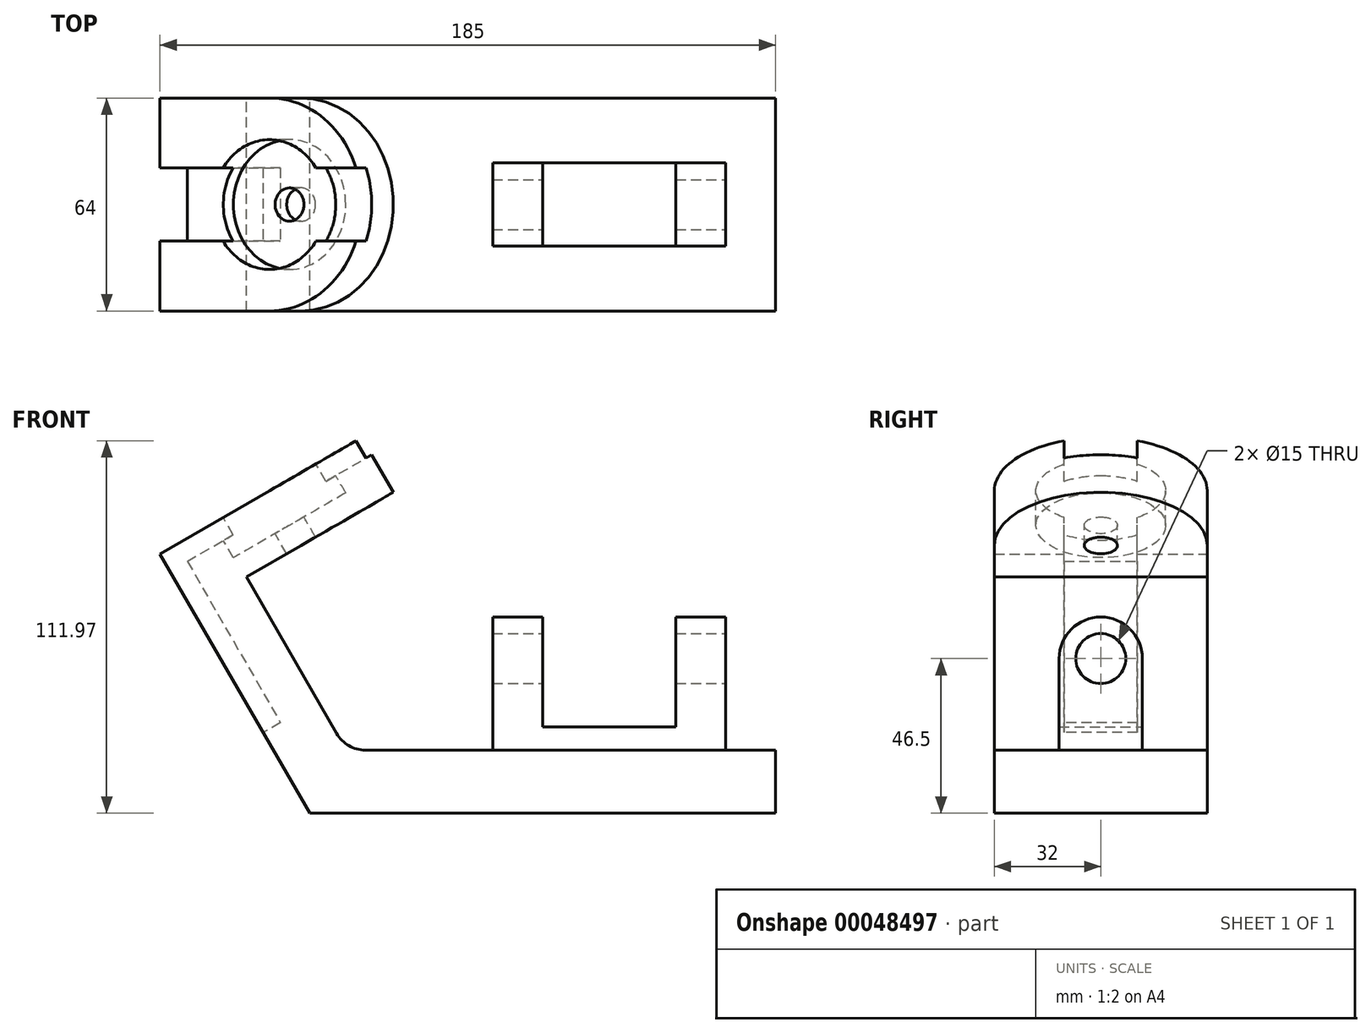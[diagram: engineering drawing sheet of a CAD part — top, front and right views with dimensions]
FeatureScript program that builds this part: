
annotation { "Feature Type Name" : "Feature", "Feature Type Description" : "" }
export const myFeature = defineFeature(function(context is Context, id is Id, definition is map)
    precondition{}
    {
        {
            var Q0;
            Q0=qCreatedBy(makeId("Front.planeOp"),FACE);
            var sketch = newSketch(context, id + "F0", { "sketchPlane" : qUnion([Q0])});
            skLineSegment(sketch, "E0", {"start": v(0, 0) * mm, "end": v(140, 0) * mm});
            skLineSegment(sketch, "E1", {"start": v(0, 0) * mm, "end": v(-45, 77.94) * mm});
            skLineSegment(sketch, "E2", {"start": v(-45, 77.94) * mm, "end": v(15.62, 112.94) * mm});
            skLineSegment(sketch, "E3.0", {"start": v(-19.05, 70.99) * mm, "end": v(25.12, 96.49) * mm});
            skLineSegment(sketch, "E3.1", {"start": v(10.97, 19) * mm, "end": v(-19.05, 70.99) * mm});
            skLineSegment(sketch, "E3.2", {"start": v(10.97, 19) * mm, "end": v(140, 19) * mm});
            skLineSegment(sketch, "E4", {"start": v(15.62, 112.94) * mm, "end": v(25.12, 96.49) * mm});
            skLineSegment(sketch, "E5", {"start": v(140, 19) * mm, "end": v(140, 0) * mm});
            skLineSegment(sketch, "E6", {"start": v(125, 19) * mm, "end": v(125, 59) * mm});
            skLineSegment(sketch, "E7", {"start": v(125, 59) * mm, "end": v(110, 59) * mm});
            skLineSegment(sketch, "E8", {"start": v(110, 59) * mm, "end": v(110, 26) * mm});
            skLineSegment(sketch, "E9", {"start": v(110, 26) * mm, "end": v(70, 26) * mm});
            skLineSegment(sketch, "E10", {"start": v(70, 26) * mm, "end": v(70, 59) * mm});
            skLineSegment(sketch, "E11", {"start": v(70, 59) * mm, "end": v(55, 59) * mm});
            skLineSegment(sketch, "E12", {"start": v(55, 59) * mm, "end": v(55, 19) * mm});
            skSolve(sketch);
        }
        {
            var Q0;
            Q0=makeQuery(id+"F0.imprint","IMPRINT",FACE,{"disambiguationData":[TD([[makeQuery(id+"F0.imprint","IMPRINT",EDGE,{"derivedFrom":sQuery(id+"F0.wireOp",EDGE,"E0")}),1.0]])]});
            extrude(context, id + "F1", {"entities" : qUnion([Q0]), "endBound" : BoundingType.SYMMETRIC, "depth" : 64 * mm});
        }
        {
            var Q0;
            {var subQ2=sQuery(id+"F0.wireOp",EDGE,"E6");Q0=makeQuery(id+"F0.imprint","IMPRINT",FACE,{"disambiguationData":[TD([[makeQuery(id+"F0.imprint","IMPRINT",EDGE,{"derivedFrom":subQ2}),1.0]])]});}
            extrude(context, id + "F2", {"entities" : qUnion([Q0]), "operationType" : NewBodyOperationType.ADD, "endBound" : BoundingType.SYMMETRIC, "depth" : 25 * mm});
        }
        {
            var Q0;
            Q0=makeQuery(id+"F1.opExtrude","SWEPT_FACE",FACE,{"disambiguationData":[OSD([sQuery(id+"F0.wireOp",EDGE,"E2")])]});
            var sketch = newSketch(context, id + "F3", { "sketchPlane" : qUnion([Q0])});
            skCircle(sketch, "E13", {"center": v(38, 0) * mm, "radius": 32 * mm});
            skSolve(sketch);
        }
        {
            var Q0;
            {var subQ0=sQuery(id+"F0.wireOp",EDGE,"E2");var subQ1=makeQuery(id+"F1.opExtrude","CAP_EDGE",EDGE,{"disambiguationData":[OSD([subQ0])],"isStart":true});var subQ2=sQuery(id+"F3.wireOp",EDGE,"E13");var subQ3=makeQuery(id+"F3.imprint","INTERSECT",VERTEX,{"derivedFrom":[subQ1,subQ2]});Q0=makeQuery(id+"F3.imprint","IMPRINT",FACE,{"disambiguationData":[TD([[makeQuery(id+"F3.imprint","IMPRINT",EDGE,{"disambiguationData":[TD([[subQ3,1.0]])],"derivedFrom":subQ2}),-1.0]])]});}
            var Q1;
            {var subQ0=sQuery(id+"F0.wireOp",EDGE,"E2");var subQ1=makeQuery(id+"F1.opExtrude","CAP_EDGE",EDGE,{"disambiguationData":[OSD([subQ0])],"isStart":false});var subQ2=sQuery(id+"F3.wireOp",EDGE,"E13");var subQ3=makeQuery(id+"F3.imprint","INTERSECT",VERTEX,{"derivedFrom":[subQ1,subQ2]});Q1=makeQuery(id+"F3.imprint","IMPRINT",FACE,{"disambiguationData":[TD([[makeQuery(id+"F3.imprint","IMPRINT",EDGE,{"disambiguationData":[TD([[subQ3,-1.0]])],"derivedFrom":subQ2}),-1.0]])]});}
            extrude(context, id + "F4", {"entities" : qUnion([Q0, Q1]), "operationType" : NewBodyOperationType.REMOVE, "endBound" : BoundingType.UP_TO_NEXT, "oppositeDirection" : true, "depth" : 25 * mm});
        }
        {
            var Q0;
            Q0=makeQuery(id+"F1.opExtrude","SWEPT_EDGE",EDGE,{"disambiguationData":[OSD([sQuery(id+"F0.wireOp",EDGE,"E3.1"),sQuery(id+"F0.wireOp",EDGE,"E3.2")])]});
            fillet(context, id + "F5", {"entities" : qUnion([Q0]), "radius" : 10 * mm, "tangentPropagation" : true, "allowEdgeOverflow" : false});
        }
        {
            var Q0;
            Q0=makeQuery(id+"F1.opExtrude","SWEPT_FACE",FACE,{"disambiguationData":[OSD([sQuery(id+"F0.wireOp",EDGE,"E2")])]});
            var sketch = newSketch(context, id + "F6", { "sketchPlane" : qUnion([Q0])});
            skCircle(sketch, "E14", {"center": v(38, 0) * mm, "radius": 19.5 * mm});
            skCircle(sketch, "E15", {"center": v(38, 0) * mm, "radius": 5 * mm});
            skSolve(sketch);
        }
        {
            var Q0;
            Q0=makeQuery(id+"F6.imprint","IMPRINT",FACE,{"disambiguationData":[TD([[makeQuery(id+"F6.imprint","IMPRINT",EDGE,{"derivedFrom":sQuery(id+"F6.wireOp",EDGE,"E15")}),1.0]])]});
            extrude(context, id + "F7", {"entities" : qUnion([Q0]), "operationType" : NewBodyOperationType.REMOVE, "endBound" : BoundingType.UP_TO_NEXT, "oppositeDirection" : true, "depth" : 25 * mm});
        }
        {
            var Q0;
            Q0=makeQuery(id+"F6.imprint","IMPRINT",FACE,{"disambiguationData":[TD([[makeQuery(id+"F6.imprint","IMPRINT",EDGE,{"derivedFrom":sQuery(id+"F6.wireOp",EDGE,"E14")}),1.0]])]});
            extrude(context, id + "F8", {"entities" : qUnion([Q0]), "operationType" : NewBodyOperationType.REMOVE, "oppositeDirection" : true, "depth" : 12 * mm});
        }
        {
            var Q0;
            Q0=makeQuery(id+"F6.imprint","IMPRINT",FACE,{"disambiguationData":[TD([[makeQuery(id+"F6.imprint","IMPRINT",EDGE,{"derivedFrom":sQuery(id+"F6.wireOp",EDGE,"E14")}),-1.0]])]});
            var sketch = newSketch(context, id + "F9", { "sketchPlane" : qUnion([Q0])});
            skLineSegment(sketch, "E16.bottom", {"start": v(0, 11) * mm, "end": v(71, 11) * mm});
            skLineSegment(sketch, "E16.top", {"start": v(0, -11) * mm, "end": v(71, -11) * mm});
            skLineSegment(sketch, "E16.left", {"start": v(0, 11) * mm, "end": v(0, -11) * mm});
            skLineSegment(sketch, "E16.right", {"start": v(71, 11) * mm, "end": v(71, -11) * mm});
            skSolve(sketch);
        }
        {
            var Q0;
            {var subQ0=makeQuery(id+"F6.imprint","IMPRINT",EDGE,{"derivedFrom":sQuery(id+"F6.wireOp",EDGE,"E14")});var subQ3=sQuery(id+"F9.wireOp",EDGE,"E16.bottom");var subQ4=makeQuery(id+"F9.imprint","INTERSECT",VERTEX,{"disambiguationData":[OD(1.0)],"derivedFrom":[subQ0,subQ3]});Q0=makeQuery(id+"F9.imprint","IMPRINT",FACE,{"disambiguationData":[TD([[makeQuery(id+"F9.imprint","IMPRINT",EDGE,{"disambiguationData":[TD([[subQ4,1.0]])],"derivedFrom":subQ0}),-1.0]])]});}
            var Q1;
            {var subQ6=sQuery(id+"F9.wireOp",EDGE,"E16.left");Q1=makeQuery(id+"F9.imprint","IMPRINT",FACE,{"disambiguationData":[TD([[makeQuery(id+"F9.imprint","IMPRINT",EDGE,{"derivedFrom":subQ6}),-1.0]])]});}
            extrude(context, id + "F10", {"entities" : qUnion([Q0, Q1]), "operationType" : NewBodyOperationType.REMOVE, "oppositeDirection" : true, "depth" : 6 * mm});
        }
        {
            var Q0;
            Q0=makeQuery(id+"F1.opExtrude","SWEPT_FACE",FACE,{"disambiguationData":[OSD([sQuery(id+"F0.wireOp",EDGE,"E1")])]});
            var sketch = newSketch(context, id + "F11", { "sketchPlane" : qUnion([Q0])});
            skLineSegment(sketch, "E17.bottom", {"start": v(-11, 84) * mm, "end": v(11, 84) * mm});
            skLineSegment(sketch, "E17.top", {"start": v(-11, 28) * mm, "end": v(11, 28) * mm});
            skLineSegment(sketch, "E17.left", {"start": v(-11, 84) * mm, "end": v(-11, 28) * mm});
            skLineSegment(sketch, "E17.right", {"start": v(11, 84) * mm, "end": v(11, 28) * mm});
            skSolve(sketch);
        }
        {
            var Q0;
            Q0=makeQuery(id+"F11.imprint","IMPRINT",FACE,{"disambiguationData":[TD([[makeQuery(id+"F11.imprint","IMPRINT",EDGE,{"derivedFrom":sQuery(id+"F11.wireOp",EDGE,"E17.bottom")}),1.0]])]});
            extrude(context, id + "F12", {"entities" : qUnion([Q0]), "operationType" : NewBodyOperationType.REMOVE, "oppositeDirection" : true, "depth" : 6 * mm});
        }
        {
            var Q0;
            Q0=makeQuery(id+"F2.opExtrude","SWEPT_FACE",FACE,{"disambiguationData":[OSD([sQuery(id+"F0.wireOp",EDGE,"E6")])]});
            var sketch = newSketch(context, id + "F13", { "sketchPlane" : qUnion([Q0])});
            skCircle(sketch, "E18", {"center": v(0, 46.5) * mm, "radius": 12.5 * mm});
            skSolve(sketch);
        }
        {
            var Q0;
            {var subQ0=sQuery(id+"F0.wireOp",EDGE,"E6");var subQ1=makeQuery(id+"F2.opExtrude","CAP_EDGE",EDGE,{"disambiguationData":[OSD([subQ0])],"isStart":false});var subQ2=sQuery(id+"F13.wireOp",EDGE,"E18");var subQ3=makeQuery(id+"F13.imprint","INTERSECT",VERTEX,{"derivedFrom":[subQ1,subQ2]});Q0=makeQuery(id+"F13.imprint","IMPRINT",FACE,{"disambiguationData":[TD([[makeQuery(id+"F13.imprint","IMPRINT",EDGE,{"disambiguationData":[TD([[subQ3,1.0]])],"derivedFrom":subQ2}),-1.0]])]});}
            var Q1;
            {var subQ0=sQuery(id+"F0.wireOp",EDGE,"E6");var subQ1=makeQuery(id+"F2.opExtrude","CAP_EDGE",EDGE,{"disambiguationData":[OSD([subQ0])],"isStart":true});var subQ2=sQuery(id+"F13.wireOp",EDGE,"E18");var subQ3=makeQuery(id+"F13.imprint","INTERSECT",VERTEX,{"derivedFrom":[subQ1,subQ2]});Q1=makeQuery(id+"F13.imprint","IMPRINT",FACE,{"disambiguationData":[TD([[makeQuery(id+"F13.imprint","IMPRINT",EDGE,{"disambiguationData":[TD([[subQ3,-1.0]])],"derivedFrom":subQ2}),-1.0]])]});}
            var Q2;
            Q2=makeQuery(id+"F2.opExtrude","SWEPT_FACE",FACE,{"disambiguationData":[OSD([sQuery(id+"F0.wireOp",EDGE,"E12")])]});
            extrude(context, id + "F14", {"entities" : qUnion([Q0, Q1]), "operationType" : NewBodyOperationType.REMOVE, "endBound" : BoundingType.UP_TO_SURFACE, "oppositeDirection" : true, "endBoundEntityFace" : qUnion([Q2]), "depth" : 25 * mm});
        }
        {
            var Q0;
            Q0=makeQuery(id+"F2.opExtrude","SWEPT_FACE",FACE,{"disambiguationData":[OSD([sQuery(id+"F0.wireOp",EDGE,"E6")])]});
            var sketch = newSketch(context, id + "F15", { "sketchPlane" : qUnion([Q0])});
            skCircle(sketch, "E19", {"center": v(0, 46.5) * mm, "radius": 7.5 * mm});
            skSolve(sketch);
        }
        {
            var Q0;
            Q0=makeQuery(id+"F15.imprint","IMPRINT",FACE,{"disambiguationData":[TD([[makeQuery(id+"F15.imprint","IMPRINT",EDGE,{"derivedFrom":sQuery(id+"F15.wireOp",EDGE,"E19")}),1.0]])]});
            var Q1;
            Q1=makeQuery(id+"F2.opExtrude","SWEPT_FACE",FACE,{"disambiguationData":[OSD([sQuery(id+"F0.wireOp",EDGE,"E12")])]});
            extrude(context, id + "F16", {"entities" : qUnion([Q0]), "operationType" : NewBodyOperationType.REMOVE, "endBound" : BoundingType.UP_TO_SURFACE, "oppositeDirection" : true, "endBoundEntityFace" : qUnion([Q1]), "depth" : 25 * mm});
        }
    });
